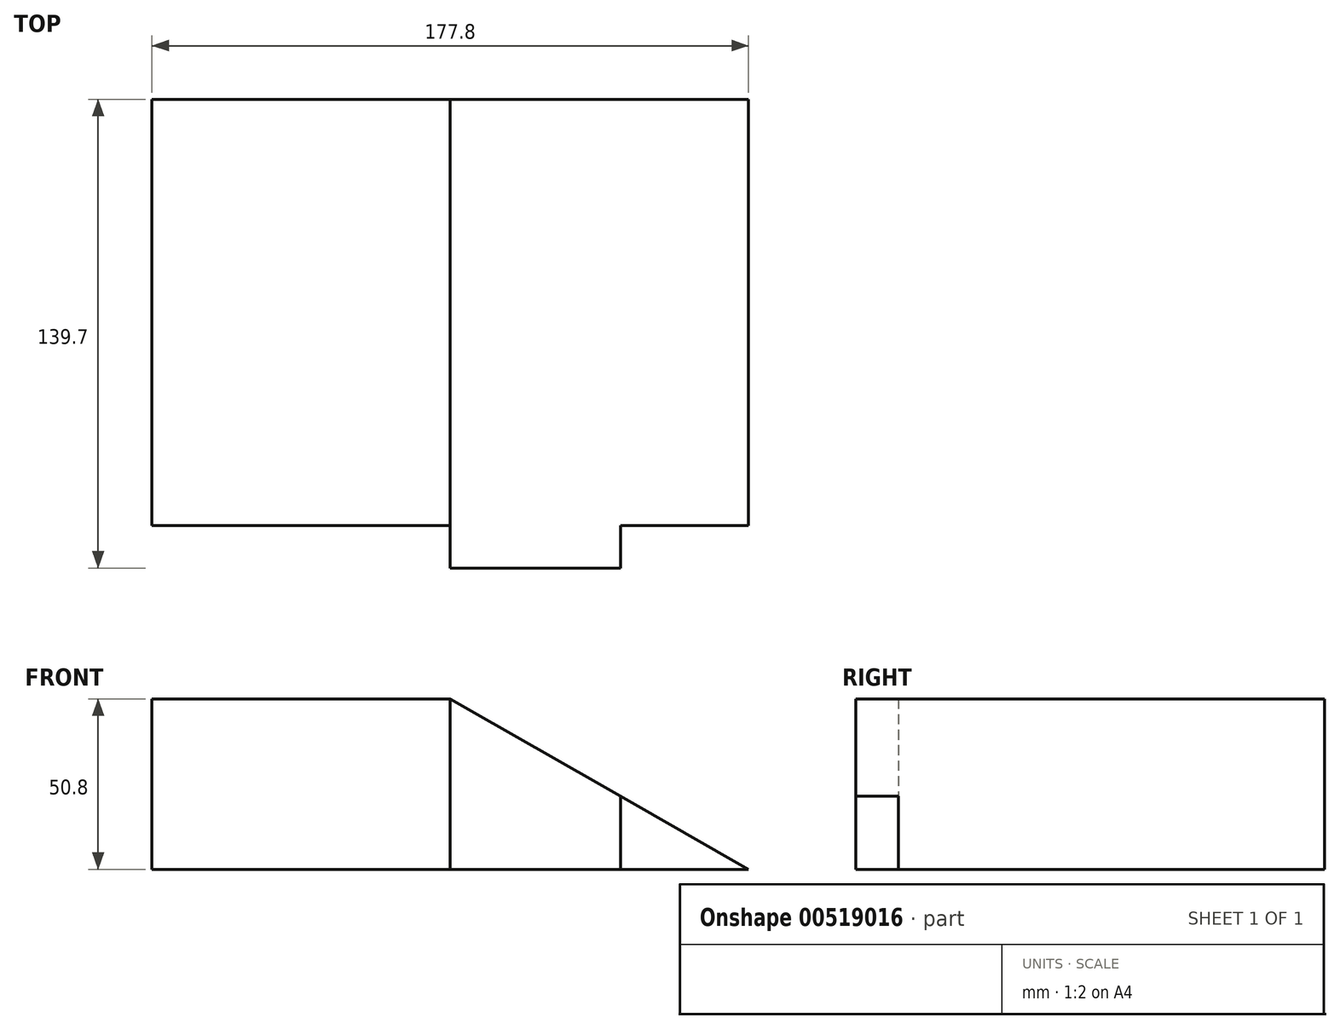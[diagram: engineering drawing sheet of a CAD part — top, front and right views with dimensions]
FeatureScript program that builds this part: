
annotation { "Feature Type Name" : "Feature", "Feature Type Description" : "" }
export const myFeature = defineFeature(function(context is Context, id is Id, definition is map)
    precondition{}
    {
        {
            var Q0;
            Q0=qCreatedBy(makeId("Top.planeOp"),FACE);
            var sketch = newSketch(context, id + "F0", { "sketchPlane" : qUnion([Q0])});
            skLineSegment(sketch, "E0.bottom", {"start": v(88.9, -63.5) * mm, "end": v(50.8, -63.5) * mm});
            skLineSegment(sketch, "E0.top", {"start": v(88.9, 63.5) * mm, "end": v(-88.9, 63.5) * mm});
            skLineSegment(sketch, "E0.left", {"start": v(88.9, -63.5) * mm, "end": v(88.9, 63.5) * mm});
            skLineSegment(sketch, "E0.right", {"start": v(-88.9, -63.5) * mm, "end": v(-88.9, 63.5) * mm});
            skPoint(sketch, "E0.middle", {"position": v(0, 0) * mm});
            skLineSegment(sketch, "E1", {"start": v(0, -63.5) * mm, "end": v(0, -76.2) * mm});
            skPoint(sketch, "E1.endSnap0", {"position": v(0, -63.5) * mm});
            skLineSegment(sketch, "E2", {"start": v(0, -76.2) * mm, "end": v(50.8, -76.2) * mm});
            skLineSegment(sketch, "E3", {"start": v(50.8, -76.2) * mm, "end": v(50.8, -63.5) * mm});
            skLineSegment(sketch, "E4.trimOffspring", {"start": v(0, -63.5) * mm, "end": v(-88.9, -63.5) * mm});
            skSolve(sketch);
        }
        {
            var Q0;
            Q0=qCreatedBy(makeId("Front.planeOp"),FACE);
            var sketch = newSketch(context, id + "F1", { "sketchPlane" : qUnion([Q0])});
            skLineSegment(sketch, "E5.bottom", {"start": v(-88.9, 0) * mm, "end": v(88.9, 0) * mm});
            skLineSegment(sketch, "E5.top", {"start": v(-88.9, 50.8) * mm, "end": v(0, 50.8) * mm});
            skLineSegment(sketch, "E5.left", {"start": v(-88.9, 0) * mm, "end": v(-88.9, 50.8) * mm});
            skLineSegment(sketch, "E6", {"start": v(50.8, 0) * mm, "end": v(50.8, 21.77) * mm});
            skLineSegment(sketch, "E7", {"start": v(0, 0) * mm, "end": v(0, 50.8) * mm, "construction": true});
            skLineSegment(sketch, "E8", {"start": v(0, 50.8) * mm, "end": v(88.9, 0) * mm});
            skSolve(sketch);
        }
        {
            var Q0;
            Q0 = qSketchRegion(id + "F0", true);
            extrude(context, id + "F2", {"entities" : qUnion([Q0]), "depth" : 50.8 * mm, "offsetDistance" : 25.4 * mm});
        }
        {
            var Q0;
            Q0 = qSketchRegion(id + "F1", true);
            extrude(context, id + "F3", {"entities" : qUnion([Q0]), "operationType" : NewBodyOperationType.INTERSECT, "endBound" : BoundingType.THROUGH_ALL, "oppositeDirection" : true, "depth" : 25.4 * mm, "offsetDistance" : 25.4 * mm, "hasSecondDirection" : true, "secondDirectionBound" : SecondDirectionBoundingType.THROUGH_ALL, "secondDirectionOppositeDirection" : false, "secondDirectionDepth" : 25.4 * mm});
        }
    });
